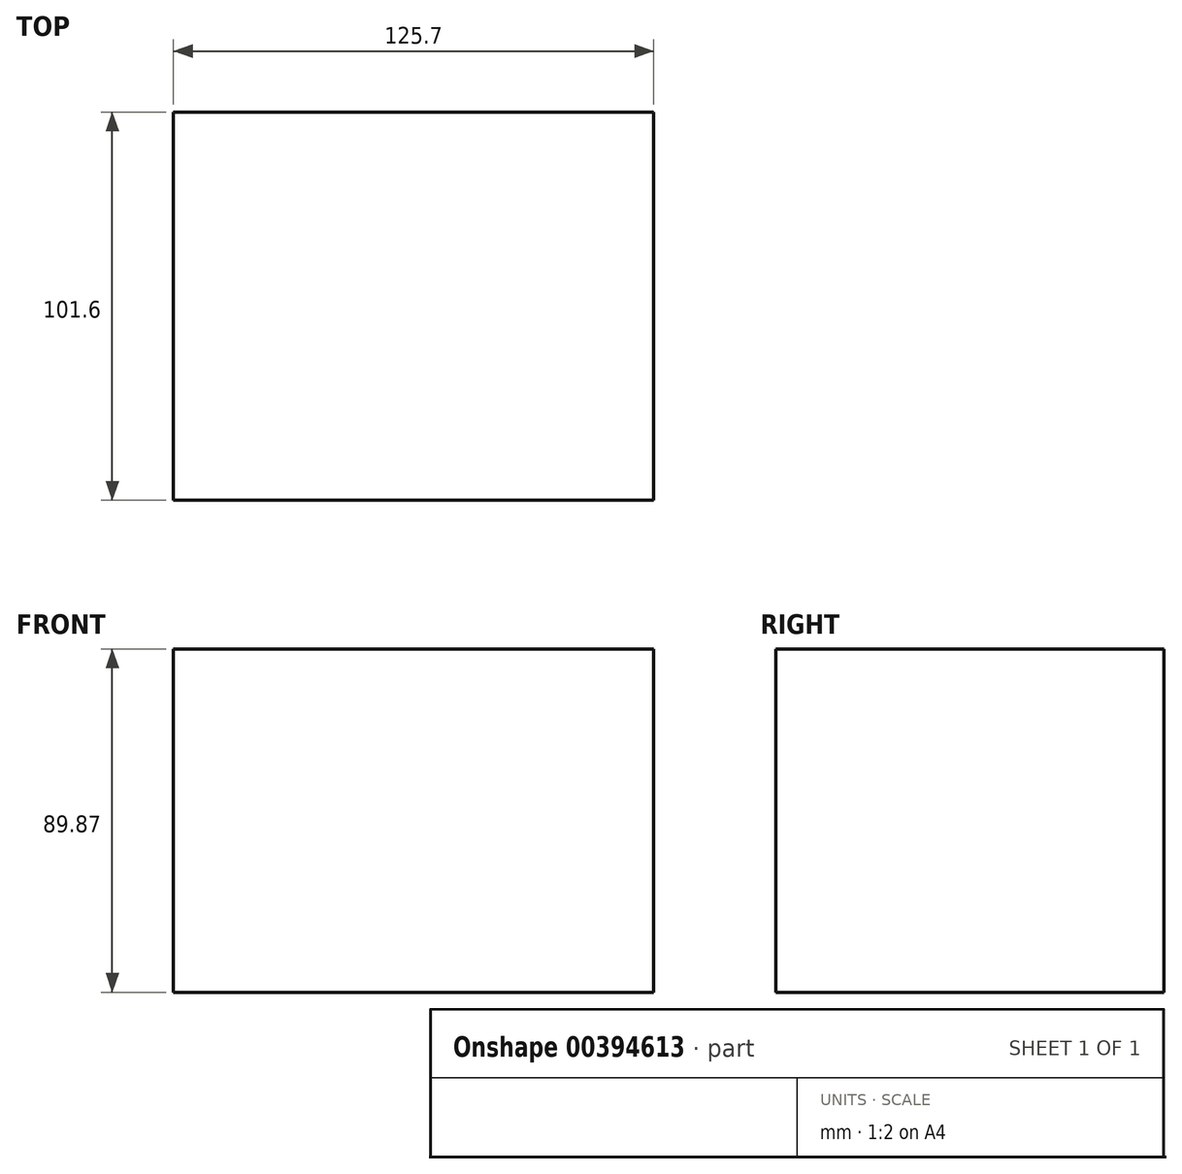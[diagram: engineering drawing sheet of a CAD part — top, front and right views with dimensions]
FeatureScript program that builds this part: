
annotation { "Feature Type Name" : "Feature", "Feature Type Description" : "" }
export const myFeature = defineFeature(function(context is Context, id is Id, definition is map)
    precondition{}
    {
        {
            var Q0;
            Q0=qCreatedBy(makeId("Front.planeOp"),FACE);
            var sketch = newSketch(context, id + "F0", { "sketchPlane" : qUnion([Q0])});
            skLineSegment(sketch, "E0.bottom", {"start": v(-60.1, 43.42) * mm, "end": v(65.6, 43.42) * mm});
            skLineSegment(sketch, "E0.top", {"start": v(-60.1, -46.45) * mm, "end": v(65.6, -46.45) * mm});
            skLineSegment(sketch, "E0.left", {"start": v(-60.1, 43.42) * mm, "end": v(-60.1, -46.45) * mm});
            skLineSegment(sketch, "E0.right", {"start": v(65.6, 43.42) * mm, "end": v(65.6, -46.45) * mm});
            skSolve(sketch);
        }
        {
            var Q0;
            Q0 = qSketchRegion(id + "F0", true);
            extrude(context, id + "F1", {"entities" : qUnion([Q0]), "depth" : 101.6 * mm});
        }
    });
